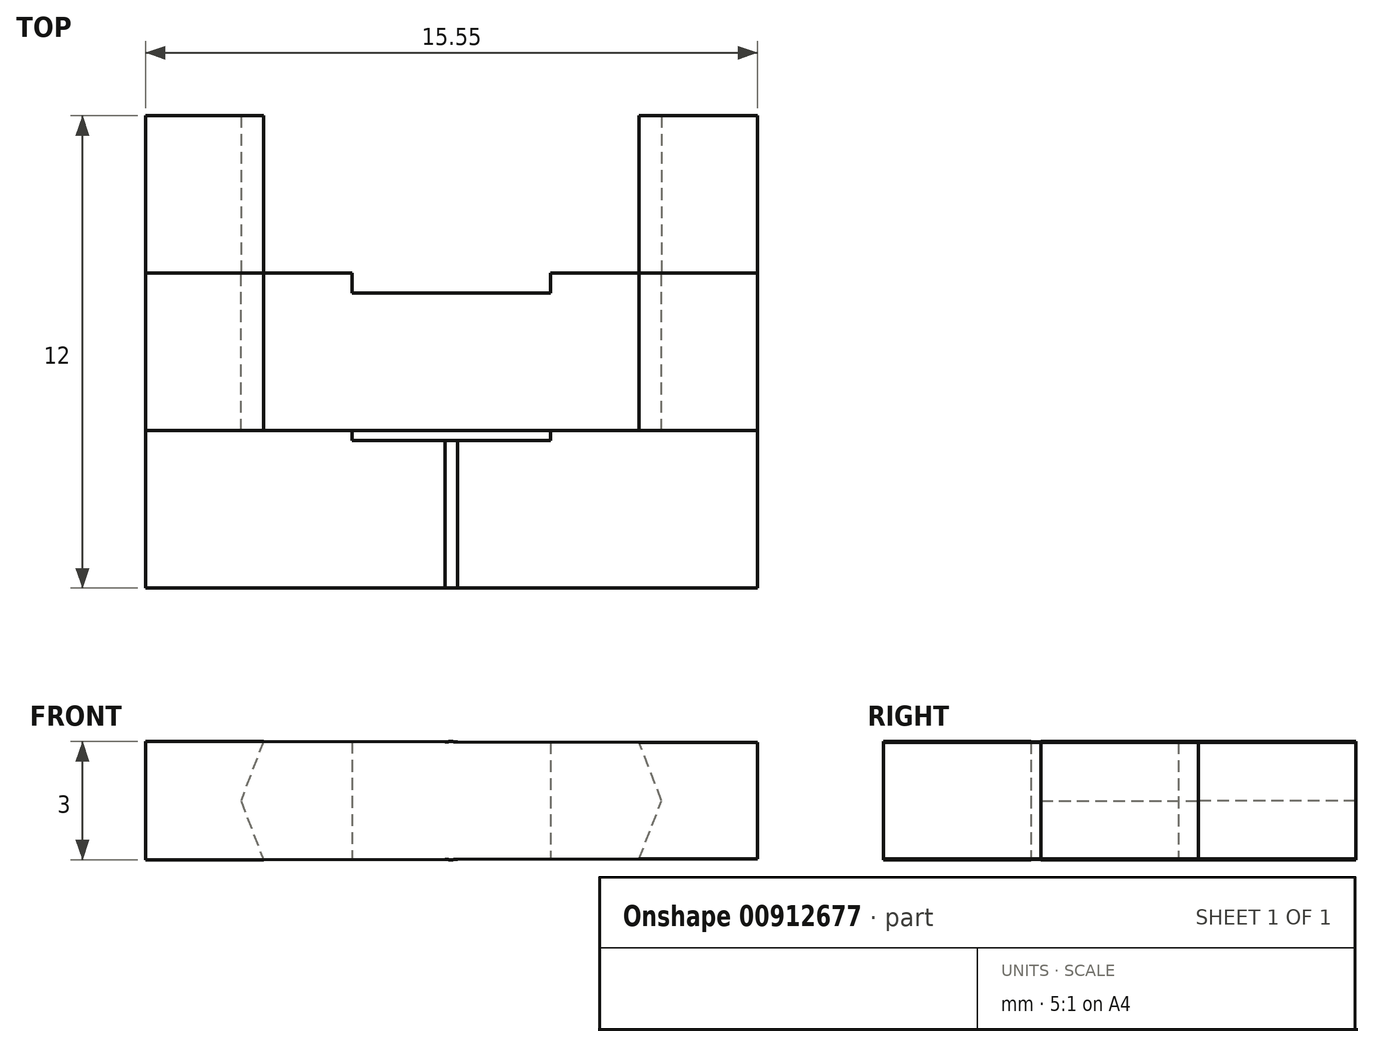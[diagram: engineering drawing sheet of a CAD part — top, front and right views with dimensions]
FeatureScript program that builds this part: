
annotation { "Feature Type Name" : "Feature", "Feature Type Description" : "" }
export const myFeature = defineFeature(function(context is Context, id is Id, definition is map)
    precondition{}
    {
        {
            var Q0;
            Q0=qCreatedBy(makeId("Front.planeOp"),FACE);
            var sketch = newSketch(context, id + "F0", { "sketchPlane" : qUnion([Q0])});
            skLineSegment(sketch, "E0", {"start": v(-4.77, 1.5) * mm, "end": v(-5.34, 0) * mm});
            skLineSegment(sketch, "E1", {"start": v(-5.34, 0) * mm, "end": v(-4.77, -1.5) * mm});
            skLineSegment(sketch, "E2", {"start": v(-4.77, -1.5) * mm, "end": v(-7.77, -1.5) * mm});
            skLineSegment(sketch, "E3", {"start": v(-7.77, -1.5) * mm, "end": v(-7.77, 1.5) * mm});
            skLineSegment(sketch, "E4", {"start": v(-7.77, 1.5) * mm, "end": v(-4.77, 1.5) * mm});
            skCircle(sketch, "E5", {"center": v(0, 0) * mm, "radius": 5 * mm});
            skCircle(sketch, "E6", {"center": v(0, 0) * mm, "radius": 1.5 * mm});
            skLineSegment(sketch, "E7", {"start": v(0, 1.5) * mm, "end": v(0, -1.5) * mm});
            skLineSegment(sketch, "E8", {"start": v(4.78, 1.48) * mm, "end": v(7.78, 1.48) * mm});
            skLineSegment(sketch, "E9", {"start": v(7.78, 1.48) * mm, "end": v(7.78, -1.48) * mm});
            skLineSegment(sketch, "E10", {"start": v(7.78, -1.48) * mm, "end": v(4.78, -1.48) * mm});
            skLineSegment(sketch, "E11", {"start": v(4.78, -1.48) * mm, "end": v(5.34, 0) * mm});
            skLineSegment(sketch, "E12", {"start": v(5.34, 0) * mm, "end": v(4.78, 1.48) * mm});
            skLineSegment(sketch, "E13", {"start": v(-4.77, 1.5) * mm, "end": v(4.78, 1.48) * mm});
            skLineSegment(sketch, "E14", {"start": v(-4.77, -1.5) * mm, "end": v(4.78, -1.48) * mm});
            skLineSegment(sketch, "E15", {"start": v(-2.53, 1.5) * mm, "end": v(-2.52, -1.5) * mm});
            skLineSegment(sketch, "E16", {"start": v(2.53, 1.49) * mm, "end": v(2.52, -1.49) * mm});
            skSolve(sketch);
        }
        {
            var Q0;
            {var subQ5=sQuery(id+"F0.wireOp",EDGE,"E16");Q0=makeQuery(id+"F0.imprint","IMPRINT",FACE,{"disambiguationData":[TD([[makeQuery(id+"F0.imprint","IMPRINT",EDGE,{"derivedFrom":subQ5}),-1.0]])]});}
            var Q1;
            Q1=makeQuery(id+"F0.imprint","IMPRINT",FACE,{"disambiguationData":[TD([[makeQuery(id+"F0.imprint","IMPRINT",EDGE,{"derivedFrom":sQuery(id+"F0.wireOp",EDGE,"E0")}),-1.0]])]});
            var Q2;
            Q2=makeQuery(id+"F0.imprint","IMPRINT",FACE,{"disambiguationData":[TD([[makeQuery(id+"F0.imprint","IMPRINT",EDGE,{"derivedFrom":sQuery(id+"F0.wireOp",EDGE,"E8")}),-1.0]])]});
            var Q3;
            {var subQ0=sQuery(id+"F0.wireOp",EDGE,"E0");Q3=makeQuery(id+"F0.imprint","IMPRINT",FACE,{"disambiguationData":[TD([[makeQuery(id+"F0.imprint","IMPRINT",EDGE,{"derivedFrom":subQ0}),1.0]])]});}
            var Q4;
            {var subQ2=sQuery(id+"F0.wireOp",EDGE,"E11");Q4=makeQuery(id+"F0.imprint","IMPRINT",FACE,{"disambiguationData":[TD([[makeQuery(id+"F0.imprint","IMPRINT",EDGE,{"derivedFrom":subQ2}),1.0]])]});}
            var Q5;
            {var subQ0=sQuery(id+"F0.wireOp",EDGE,"E13");var subQ5=sQuery(id+"F0.wireOp",EDGE,"E15");var subQ6=makeQuery(id+"F0.imprint","INTERSECT",VERTEX,{"derivedFrom":[subQ0,subQ5]});Q5=makeQuery(id+"F0.imprint","IMPRINT",FACE,{"disambiguationData":[TD([[makeQuery(id+"F0.imprint","IMPRINT",EDGE,{"disambiguationData":[TD([[subQ6,-1.0]])],"derivedFrom":subQ5}),-1.0]])]});}
            var Q6;
            {var subQ5=sQuery(id+"F0.wireOp",EDGE,"E16");Q6=makeQuery(id+"F0.imprint","IMPRINT",FACE,{"disambiguationData":[TD([[makeQuery(id+"F0.imprint","IMPRINT",EDGE,{"derivedFrom":subQ5}),1.0]])]});}
            var Q7;
            {var subQ0=sQuery(id+"F0.wireOp",EDGE,"E13");var subQ1=sQuery(id+"F0.wireOp",EDGE,"E6");var subQ2=makeQuery(id+"F0.imprint","INTERSECT",VERTEX,{"disambiguationData":[OD(1.0)],"derivedFrom":[subQ1,subQ0]});Q7=makeQuery(id+"F0.imprint","IMPRINT",FACE,{"disambiguationData":[TD([[makeQuery(id+"F0.imprint","IMPRINT",EDGE,{"disambiguationData":[TD([[subQ2,-1.0]])],"derivedFrom":subQ1}),1.0]])]});}
            var Q8;
            {var subQ0=sQuery(id+"F0.wireOp",EDGE,"E13");var subQ1=sQuery(id+"F0.wireOp",EDGE,"E6");var subQ2=makeQuery(id+"F0.imprint","INTERSECT",VERTEX,{"disambiguationData":[OD(1.0)],"derivedFrom":[subQ1,subQ0]});Q8=makeQuery(id+"F0.imprint","IMPRINT",FACE,{"disambiguationData":[TD([[makeQuery(id+"F0.imprint","IMPRINT",EDGE,{"disambiguationData":[TD([[subQ2,-1.0]])],"derivedFrom":subQ1}),-1.0]])]});}
            var Q9;
            {var subQ0=sQuery(id+"F0.wireOp",EDGE,"E13");var subQ1=sQuery(id+"F0.wireOp",EDGE,"E6");var subQ2=makeQuery(id+"F0.imprint","INTERSECT",VERTEX,{"disambiguationData":[OD(0.0)],"derivedFrom":[subQ1,subQ0]});Q9=makeQuery(id+"F0.imprint","IMPRINT",FACE,{"disambiguationData":[TD([[makeQuery(id+"F0.imprint","IMPRINT",EDGE,{"disambiguationData":[TD([[subQ2,1.0]])],"derivedFrom":subQ1}),1.0]])]});}
            var Q10;
            {var subQ0=sQuery(id+"F0.wireOp",EDGE,"E7");var subQ1=sQuery(id+"F0.wireOp",EDGE,"E6");var subQ2=makeQuery(id+"F0.imprint","INTERSECT",VERTEX,{"disambiguationData":[OD(0.0)],"derivedFrom":[subQ1,subQ0]});Q10=makeQuery(id+"F0.imprint","IMPRINT",FACE,{"disambiguationData":[TD([[makeQuery(id+"F0.imprint","IMPRINT",EDGE,{"disambiguationData":[TD([[subQ2,1.0]])],"derivedFrom":subQ1}),1.0]])]});}
            var Q11;
            {var subQ0=sQuery(id+"F0.wireOp",EDGE,"E7");var subQ1=sQuery(id+"F0.wireOp",EDGE,"E6");var subQ2=makeQuery(id+"F0.imprint","INTERSECT",VERTEX,{"disambiguationData":[OD(0.0)],"derivedFrom":[subQ1,subQ0]});Q11=makeQuery(id+"F0.imprint","IMPRINT",FACE,{"disambiguationData":[TD([[makeQuery(id+"F0.imprint","IMPRINT",EDGE,{"disambiguationData":[TD([[subQ2,-1.0]])],"derivedFrom":subQ1}),1.0]])]});}
            var Q12;
            {var subQ0=sQuery(id+"F0.wireOp",EDGE,"E7");var subQ1=sQuery(id+"F0.wireOp",EDGE,"E6");var subQ2=makeQuery(id+"F0.imprint","INTERSECT",VERTEX,{"disambiguationData":[OD(1.0)],"derivedFrom":[subQ1,subQ0]});Q12=makeQuery(id+"F0.imprint","IMPRINT",FACE,{"disambiguationData":[TD([[makeQuery(id+"F0.imprint","IMPRINT",EDGE,{"disambiguationData":[TD([[subQ2,1.0]])],"derivedFrom":subQ1}),1.0]])]});}
            var Q13;
            {var subQ0=sQuery(id+"F0.wireOp",EDGE,"E7");var subQ1=sQuery(id+"F0.wireOp",EDGE,"E6");var subQ2=makeQuery(id+"F0.imprint","INTERSECT",VERTEX,{"disambiguationData":[OD(1.0)],"derivedFrom":[subQ1,subQ0]});Q13=makeQuery(id+"F0.imprint","IMPRINT",FACE,{"disambiguationData":[TD([[makeQuery(id+"F0.imprint","IMPRINT",EDGE,{"disambiguationData":[TD([[subQ2,-1.0]])],"derivedFrom":subQ1}),1.0]])]});}
            extrude(context, id + "F1", {"entities" : qUnion([Q0, Q1, Q2, Q3, Q4, Q5, Q6, Q7, Q8, Q9, Q10, Q11, Q12, Q13]), "depth" : 8 * mm, "offsetDistance" : 25 * mm});
        }
        {
            var Q0;
            {var subQ2=sQuery(id+"F0.wireOp",EDGE,"E11");Q0=makeQuery(id+"F0.imprint","IMPRINT",FACE,{"disambiguationData":[TD([[makeQuery(id+"F0.imprint","IMPRINT",EDGE,{"derivedFrom":subQ2}),1.0]])]});}
            var Q1;
            {var subQ5=sQuery(id+"F0.wireOp",EDGE,"E16");Q1=makeQuery(id+"F0.imprint","IMPRINT",FACE,{"disambiguationData":[TD([[makeQuery(id+"F0.imprint","IMPRINT",EDGE,{"derivedFrom":subQ5}),1.0]])]});}
            var Q2;
            {var subQ5=sQuery(id+"F0.wireOp",EDGE,"E16");Q2=makeQuery(id+"F0.imprint","IMPRINT",FACE,{"disambiguationData":[TD([[makeQuery(id+"F0.imprint","IMPRINT",EDGE,{"derivedFrom":subQ5}),-1.0]])]});}
            var Q3;
            {var subQ0=sQuery(id+"F0.wireOp",EDGE,"E13");var subQ1=sQuery(id+"F0.wireOp",EDGE,"E6");var subQ2=makeQuery(id+"F0.imprint","INTERSECT",VERTEX,{"disambiguationData":[OD(0.0)],"derivedFrom":[subQ1,subQ0]});Q3=makeQuery(id+"F0.imprint","IMPRINT",FACE,{"disambiguationData":[TD([[makeQuery(id+"F0.imprint","IMPRINT",EDGE,{"disambiguationData":[TD([[subQ2,1.0]])],"derivedFrom":subQ1}),1.0]])]});}
            var Q4;
            {var subQ0=sQuery(id+"F0.wireOp",EDGE,"E13");var subQ1=sQuery(id+"F0.wireOp",EDGE,"E6");var subQ2=makeQuery(id+"F0.imprint","INTERSECT",VERTEX,{"disambiguationData":[OD(1.0)],"derivedFrom":[subQ1,subQ0]});Q4=makeQuery(id+"F0.imprint","IMPRINT",FACE,{"disambiguationData":[TD([[makeQuery(id+"F0.imprint","IMPRINT",EDGE,{"disambiguationData":[TD([[subQ2,-1.0]])],"derivedFrom":subQ1}),1.0]])]});}
            var Q5;
            {var subQ0=sQuery(id+"F0.wireOp",EDGE,"E13");var subQ1=sQuery(id+"F0.wireOp",EDGE,"E6");var subQ2=makeQuery(id+"F0.imprint","INTERSECT",VERTEX,{"disambiguationData":[OD(1.0)],"derivedFrom":[subQ1,subQ0]});Q5=makeQuery(id+"F0.imprint","IMPRINT",FACE,{"disambiguationData":[TD([[makeQuery(id+"F0.imprint","IMPRINT",EDGE,{"disambiguationData":[TD([[subQ2,-1.0]])],"derivedFrom":subQ1}),-1.0]])]});}
            var Q6;
            {var subQ0=sQuery(id+"F0.wireOp",EDGE,"E13");var subQ5=sQuery(id+"F0.wireOp",EDGE,"E15");var subQ6=makeQuery(id+"F0.imprint","INTERSECT",VERTEX,{"derivedFrom":[subQ0,subQ5]});Q6=makeQuery(id+"F0.imprint","IMPRINT",FACE,{"disambiguationData":[TD([[makeQuery(id+"F0.imprint","IMPRINT",EDGE,{"disambiguationData":[TD([[subQ6,-1.0]])],"derivedFrom":subQ5}),-1.0]])]});}
            var Q7;
            {var subQ0=sQuery(id+"F0.wireOp",EDGE,"E0");Q7=makeQuery(id+"F0.imprint","IMPRINT",FACE,{"disambiguationData":[TD([[makeQuery(id+"F0.imprint","IMPRINT",EDGE,{"derivedFrom":subQ0}),1.0]])]});}
            extrude(context, id + "F2", {"entities" : qUnion([Q0, Q1, Q2, Q3, Q4, Q5, Q6, Q7]), "operationType" : NewBodyOperationType.REMOVE, "oppositeDirection" : true, "depth" : -4 * mm, "offsetDistance" : 25 * mm});
        }
        {
            var Q0;
            {var subQ5=sQuery(id+"F0.wireOp",EDGE,"E16");Q0=makeQuery(id+"F0.imprint","IMPRINT",FACE,{"disambiguationData":[TD([[makeQuery(id+"F0.imprint","IMPRINT",EDGE,{"derivedFrom":subQ5}),-1.0]])]});}
            var Q1;
            {var subQ0=sQuery(id+"F0.wireOp",EDGE,"E13");var subQ1=sQuery(id+"F0.wireOp",EDGE,"E6");var subQ2=makeQuery(id+"F0.imprint","INTERSECT",VERTEX,{"disambiguationData":[OD(0.0)],"derivedFrom":[subQ1,subQ0]});Q1=makeQuery(id+"F0.imprint","IMPRINT",FACE,{"disambiguationData":[TD([[makeQuery(id+"F0.imprint","IMPRINT",EDGE,{"disambiguationData":[TD([[subQ2,1.0]])],"derivedFrom":subQ1}),1.0]])]});}
            var Q2;
            {var subQ0=sQuery(id+"F0.wireOp",EDGE,"E13");var subQ1=sQuery(id+"F0.wireOp",EDGE,"E6");var subQ2=makeQuery(id+"F0.imprint","INTERSECT",VERTEX,{"disambiguationData":[OD(1.0)],"derivedFrom":[subQ1,subQ0]});Q2=makeQuery(id+"F0.imprint","IMPRINT",FACE,{"disambiguationData":[TD([[makeQuery(id+"F0.imprint","IMPRINT",EDGE,{"disambiguationData":[TD([[subQ2,-1.0]])],"derivedFrom":subQ1}),-1.0]])]});}
            var Q3;
            {var subQ0=sQuery(id+"F0.wireOp",EDGE,"E13");var subQ1=sQuery(id+"F0.wireOp",EDGE,"E6");var subQ2=makeQuery(id+"F0.imprint","INTERSECT",VERTEX,{"disambiguationData":[OD(1.0)],"derivedFrom":[subQ1,subQ0]});Q3=makeQuery(id+"F0.imprint","IMPRINT",FACE,{"disambiguationData":[TD([[makeQuery(id+"F0.imprint","IMPRINT",EDGE,{"disambiguationData":[TD([[subQ2,-1.0]])],"derivedFrom":subQ1}),1.0]])]});}
            var Q4;
            {var subQ0=sQuery(id+"F0.wireOp",EDGE,"E7");var subQ1=sQuery(id+"F0.wireOp",EDGE,"E6");var subQ2=makeQuery(id+"F0.imprint","INTERSECT",VERTEX,{"disambiguationData":[OD(0.0)],"derivedFrom":[subQ1,subQ0]});Q4=makeQuery(id+"F0.imprint","IMPRINT",FACE,{"disambiguationData":[TD([[makeQuery(id+"F0.imprint","IMPRINT",EDGE,{"disambiguationData":[TD([[subQ2,-1.0]])],"derivedFrom":subQ1}),1.0]])]});}
            var Q5;
            {var subQ0=sQuery(id+"F0.wireOp",EDGE,"E7");var subQ1=sQuery(id+"F0.wireOp",EDGE,"E6");var subQ2=makeQuery(id+"F0.imprint","INTERSECT",VERTEX,{"disambiguationData":[OD(0.0)],"derivedFrom":[subQ1,subQ0]});Q5=makeQuery(id+"F0.imprint","IMPRINT",FACE,{"disambiguationData":[TD([[makeQuery(id+"F0.imprint","IMPRINT",EDGE,{"disambiguationData":[TD([[subQ2,1.0]])],"derivedFrom":subQ1}),1.0]])]});}
            var Q6;
            {var subQ0=sQuery(id+"F0.wireOp",EDGE,"E7");var subQ1=sQuery(id+"F0.wireOp",EDGE,"E6");var subQ2=makeQuery(id+"F0.imprint","INTERSECT",VERTEX,{"disambiguationData":[OD(1.0)],"derivedFrom":[subQ1,subQ0]});Q6=makeQuery(id+"F0.imprint","IMPRINT",FACE,{"disambiguationData":[TD([[makeQuery(id+"F0.imprint","IMPRINT",EDGE,{"disambiguationData":[TD([[subQ2,-1.0]])],"derivedFrom":subQ1}),1.0]])]});}
            var Q7;
            {var subQ0=sQuery(id+"F0.wireOp",EDGE,"E7");var subQ1=sQuery(id+"F0.wireOp",EDGE,"E6");var subQ2=makeQuery(id+"F0.imprint","INTERSECT",VERTEX,{"disambiguationData":[OD(1.0)],"derivedFrom":[subQ1,subQ0]});Q7=makeQuery(id+"F0.imprint","IMPRINT",FACE,{"disambiguationData":[TD([[makeQuery(id+"F0.imprint","IMPRINT",EDGE,{"disambiguationData":[TD([[subQ2,1.0]])],"derivedFrom":subQ1}),1.0]])]});}
            extrude(context, id + "F3", {"entities" : qUnion([Q0, Q1, Q2, Q3, Q4, Q5, Q6, Q7]), "operationType" : NewBodyOperationType.REMOVE, "oppositeDirection" : true, "depth" : -4.25 * mm, "offsetDistance" : 25 * mm});
        }
        {
            var Q0;
            Q0=makeQuery(id+"F0.imprint","IMPRINT",FACE,{"disambiguationData":[TD([[makeQuery(id+"F0.imprint","IMPRINT",EDGE,{"derivedFrom":sQuery(id+"F0.wireOp",EDGE,"E0")}),-1.0]])]});
            var Q1;
            Q1=makeQuery(id+"F0.imprint","IMPRINT",FACE,{"disambiguationData":[TD([[makeQuery(id+"F0.imprint","IMPRINT",EDGE,{"derivedFrom":sQuery(id+"F0.wireOp",EDGE,"E8")}),-1.0]])]});
            extrude(context, id + "F4", {"entities" : qUnion([Q0, Q1]), "depth" : -4 * mm, "offsetDistance" : 25 * mm});
        }
        {
            var Q0;
            Q0=makeQuery(id+"F4.opExtrude","CAP_FACE",FACE,{"disambiguationData":[OSD([sQuery(id+"F0.wireOp",EDGE,"E0"),sQuery(id+"F0.wireOp",EDGE,"E1"),sQuery(id+"F0.wireOp",EDGE,"E2"),sQuery(id+"F0.wireOp",EDGE,"E3"),sQuery(id+"F0.wireOp",EDGE,"E4")])],"isStart":true});
            var Q1;
            {var subQ0=sQuery(id+"F0.wireOp",EDGE,"E0");Q1=makeQuery(id+"F0.imprint","IMPRINT",FACE,{"disambiguationData":[TD([[makeQuery(id+"F0.imprint","IMPRINT",EDGE,{"derivedFrom":subQ0}),1.0]])]});}
            var Q2;
            {var subQ0=sQuery(id+"F0.wireOp",EDGE,"E13");var subQ5=sQuery(id+"F0.wireOp",EDGE,"E15");var subQ6=makeQuery(id+"F0.imprint","INTERSECT",VERTEX,{"derivedFrom":[subQ0,subQ5]});Q2=makeQuery(id+"F0.imprint","IMPRINT",FACE,{"disambiguationData":[TD([[makeQuery(id+"F0.imprint","IMPRINT",EDGE,{"disambiguationData":[TD([[subQ6,-1.0]])],"derivedFrom":subQ5}),-1.0]])]});}
            var Q3;
            {var subQ0=sQuery(id+"F0.wireOp",EDGE,"E13");var subQ1=sQuery(id+"F0.wireOp",EDGE,"E6");var subQ2=makeQuery(id+"F0.imprint","INTERSECT",VERTEX,{"disambiguationData":[OD(1.0)],"derivedFrom":[subQ1,subQ0]});Q3=makeQuery(id+"F0.imprint","IMPRINT",FACE,{"disambiguationData":[TD([[makeQuery(id+"F0.imprint","IMPRINT",EDGE,{"disambiguationData":[TD([[subQ2,-1.0]])],"derivedFrom":subQ1}),-1.0]])]});}
            var Q4;
            {var subQ0=sQuery(id+"F0.wireOp",EDGE,"E13");var subQ1=sQuery(id+"F0.wireOp",EDGE,"E6");var subQ2=makeQuery(id+"F0.imprint","INTERSECT",VERTEX,{"disambiguationData":[OD(1.0)],"derivedFrom":[subQ1,subQ0]});Q4=makeQuery(id+"F0.imprint","IMPRINT",FACE,{"disambiguationData":[TD([[makeQuery(id+"F0.imprint","IMPRINT",EDGE,{"disambiguationData":[TD([[subQ2,-1.0]])],"derivedFrom":subQ1}),1.0]])]});}
            var Q5;
            {var subQ0=sQuery(id+"F0.wireOp",EDGE,"E13");var subQ1=sQuery(id+"F0.wireOp",EDGE,"E6");var subQ2=makeQuery(id+"F0.imprint","INTERSECT",VERTEX,{"disambiguationData":[OD(0.0)],"derivedFrom":[subQ1,subQ0]});Q5=makeQuery(id+"F0.imprint","IMPRINT",FACE,{"disambiguationData":[TD([[makeQuery(id+"F0.imprint","IMPRINT",EDGE,{"disambiguationData":[TD([[subQ2,1.0]])],"derivedFrom":subQ1}),1.0]])]});}
            var Q6;
            {var subQ5=sQuery(id+"F0.wireOp",EDGE,"E16");Q6=makeQuery(id+"F0.imprint","IMPRINT",FACE,{"disambiguationData":[TD([[makeQuery(id+"F0.imprint","IMPRINT",EDGE,{"derivedFrom":subQ5}),-1.0]])]});}
            var Q7;
            {var subQ5=sQuery(id+"F0.wireOp",EDGE,"E16");Q7=makeQuery(id+"F0.imprint","IMPRINT",FACE,{"disambiguationData":[TD([[makeQuery(id+"F0.imprint","IMPRINT",EDGE,{"derivedFrom":subQ5}),1.0]])]});}
            var Q8;
            {var subQ2=sQuery(id+"F0.wireOp",EDGE,"E11");Q8=makeQuery(id+"F0.imprint","IMPRINT",FACE,{"disambiguationData":[TD([[makeQuery(id+"F0.imprint","IMPRINT",EDGE,{"derivedFrom":subQ2}),1.0]])]});}
            var Q9;
            Q9=makeQuery(id+"F0.imprint","IMPRINT",FACE,{"disambiguationData":[TD([[makeQuery(id+"F0.imprint","IMPRINT",EDGE,{"derivedFrom":sQuery(id+"F0.wireOp",EDGE,"E8")}),-1.0]])]});
            extrude(context, id + "F5", {"entities" : qUnion([Q0, Q1, Q2, Q3, Q4, Q5, Q6, Q7, Q8, Q9]), "depth" : 4 * mm, "offsetDistance" : 25 * mm});
        }
        {
            var Q0;
            {var subQ0=sQuery(id+"F0.wireOp",EDGE,"E13");var subQ1=sQuery(id+"F0.wireOp",EDGE,"E6");var subQ2=makeQuery(id+"F0.imprint","INTERSECT",VERTEX,{"disambiguationData":[OD(1.0)],"derivedFrom":[subQ1,subQ0]});Q0=makeQuery(id+"F0.imprint","IMPRINT",FACE,{"disambiguationData":[TD([[makeQuery(id+"F0.imprint","IMPRINT",EDGE,{"disambiguationData":[TD([[subQ2,-1.0]])],"derivedFrom":subQ1}),-1.0]])]});}
            var Q1;
            {var subQ0=sQuery(id+"F0.wireOp",EDGE,"E13");var subQ1=sQuery(id+"F0.wireOp",EDGE,"E6");var subQ2=makeQuery(id+"F0.imprint","INTERSECT",VERTEX,{"disambiguationData":[OD(1.0)],"derivedFrom":[subQ1,subQ0]});Q1=makeQuery(id+"F0.imprint","IMPRINT",FACE,{"disambiguationData":[TD([[makeQuery(id+"F0.imprint","IMPRINT",EDGE,{"disambiguationData":[TD([[subQ2,-1.0]])],"derivedFrom":subQ1}),1.0]])]});}
            var Q2;
            {var subQ0=sQuery(id+"F0.wireOp",EDGE,"E13");var subQ1=sQuery(id+"F0.wireOp",EDGE,"E6");var subQ2=makeQuery(id+"F0.imprint","INTERSECT",VERTEX,{"disambiguationData":[OD(0.0)],"derivedFrom":[subQ1,subQ0]});Q2=makeQuery(id+"F0.imprint","IMPRINT",FACE,{"disambiguationData":[TD([[makeQuery(id+"F0.imprint","IMPRINT",EDGE,{"disambiguationData":[TD([[subQ2,1.0]])],"derivedFrom":subQ1}),1.0]])]});}
            var Q3;
            {var subQ5=sQuery(id+"F0.wireOp",EDGE,"E16");Q3=makeQuery(id+"F0.imprint","IMPRINT",FACE,{"disambiguationData":[TD([[makeQuery(id+"F0.imprint","IMPRINT",EDGE,{"derivedFrom":subQ5}),-1.0]])]});}
            extrude(context, id + "F6", {"entities" : qUnion([Q0, Q1, Q2, Q3]), "operationType" : NewBodyOperationType.REMOVE, "oppositeDirection" : true, "depth" : -0.5 * mm, "offsetDistance" : 25 * mm});
        }
    });
